# Revit family: Single-Flush with ADA Clearance
name_source: partatom
category: Doors
revit_build: Autodesk Revit LT 2014 (Build: 20130308_1515)
units: mm (PartAtom-declared; Revit-internal decimal feet)

## types (7) — shared parameters
Analytic Construction = Metal
Assembly Code = C1020
Construction Type Id = MDOOR
Door Material = Door - Panel
Frame Material = Door - Frame
Function = Interior
Heat Transfer Coefficient (U) = 0.6520 BTU/(h·ft²·°F)
Thermal Resistance (R) = 1.5338 (h·ft²·°F)/BTU
Trim Projection Ext = 0' - 1"
Trim Projection Int = 0' - 1"
Trim Width = 0' - 3"
Wall Closure = By host
zero-valued in all types: Solar Heat Gain Coefficient, Visual Light Transmittance

## per-type parameters (varying)
| type | Height | Thickness | Width |
| 36" x 84" | 7' - 0" | 0' - 4" | 3' - 0" |
| 34" x 84" | 7' - 0" | 0' - 2" | 2' - 10" |
| 32" x 84" | 7' - 0" | 0' - 2" | 2' - 8" |
| 30" x 84" | 7' - 0" | 0' - 2" | 2' - 6" |
| 30" x 80" | 6' - 8" | 0' - 2" | 2' - 6" |
| 36" x 80" | 6' - 8" | 0' - 2" | 3' - 0" |
| 34" x 80" | 6' - 8" | 0' - 2" | 2' - 10" |

## geometry (parser evidence)
native form markers: Blend x4, Sweep x6
no freeform markers — native parametric forms only
